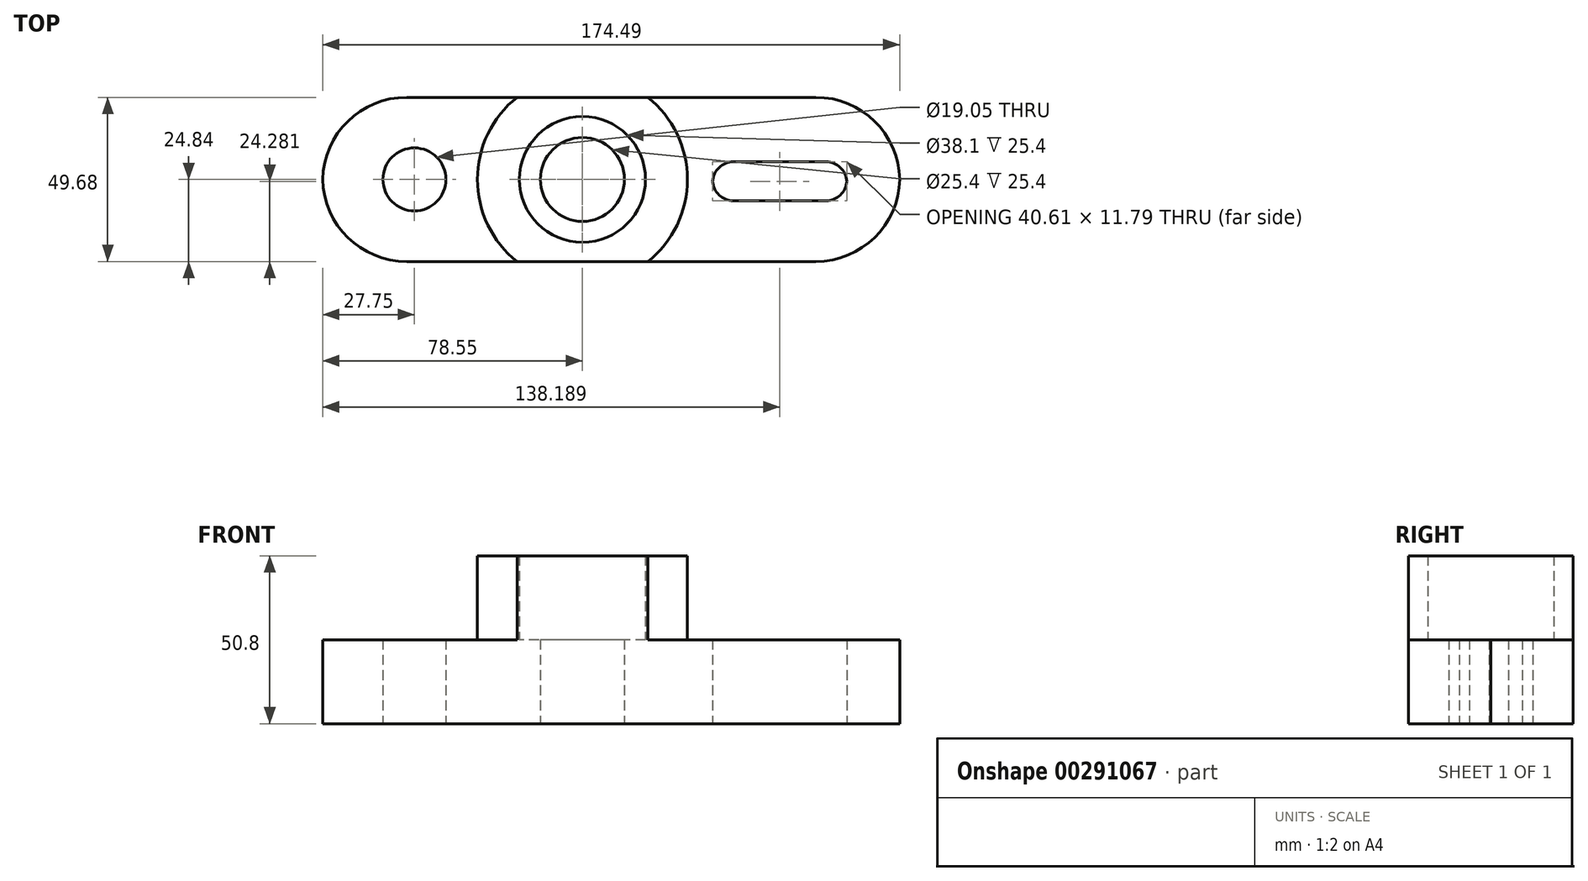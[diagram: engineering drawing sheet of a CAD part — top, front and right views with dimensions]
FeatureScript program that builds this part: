
annotation { "Feature Type Name" : "Feature", "Feature Type Description" : "" }
export const myFeature = defineFeature(function(context is Context, id is Id, definition is map)
    precondition{}
    {
        {
            var Q0;
            Q0=qCreatedBy(makeId("Top.planeOp"),FACE);
            var sketch = newSketch(context, id + "F0", { "sketchPlane" : qUnion([Q0])});
            skCircle(sketch, "E0", {"center": v(0, 0) * mm, "radius": 12.7 * mm});
            skCircle(sketch, "E1", {"center": v(0, 0) * mm, "radius": 19.05 * mm});
            skCircle(sketch, "E2", {"center": v(0, 0) * mm, "radius": 31.75 * mm});
            skCircle(sketch, "E3", {"center": v(-50.8, 0) * mm, "radius": 9.53 * mm});
            skLineSegment(sketch, "E4.bottom", {"start": v(-53.16, 24.84) * mm, "end": v(70.55, 24.84) * mm});
            skLineSegment(sketch, "E4.top", {"start": v(-53.16, -24.84) * mm, "end": v(70.55, -24.84) * mm});
            skArc(sketch, "E5.filletArc", {"start": v(-53.16, 24.84) * mm, "mid": v(-70.92, 17.6) * mm, "end": v(-78.55, 0) * mm});
            skArc(sketch, "E6.filletArc", {"start": v(-78.55, 0) * mm, "mid": v(-70.92, -17.6) * mm, "end": v(-53.16, -24.84) * mm});
            skArc(sketch, "E7.filletArc", {"start": v(95.94, 0) * mm, "mid": v(88.31, 17.6) * mm, "end": v(70.55, 24.84) * mm});
            skArc(sketch, "E8.filletArc", {"start": v(70.55, -24.84) * mm, "mid": v(88.31, -17.6) * mm, "end": v(95.94, 0) * mm});
            skLineSegment(sketch, "E9.bottom", {"start": v(45.67, 5.33) * mm, "end": v(73.6, 5.33) * mm});
            skLineSegment(sketch, "E9.top", {"start": v(45.67, -6.45) * mm, "end": v(73.6, -6.45) * mm});
            skArc(sketch, "E10.filletArc", {"start": v(45.67, 5.33) * mm, "mid": v(41.34, 3.63) * mm, "end": v(39.34, -0.56) * mm});
            skArc(sketch, "E11.filletArc", {"start": v(39.34, -0.56) * mm, "mid": v(41.34, -4.75) * mm, "end": v(45.67, -6.45) * mm});
            skArc(sketch, "E12.filletArc", {"start": v(79.94, -0.56) * mm, "mid": v(77.93, 3.63) * mm, "end": v(73.6, 5.33) * mm});
            skArc(sketch, "E13.filletArc", {"start": v(73.6, -6.45) * mm, "mid": v(77.93, -4.75) * mm, "end": v(79.94, -0.56) * mm});
            skSolve(sketch);
        }
        {
            var Q0;
            Q0=makeQuery(id+"F0.imprint","IMPRINT",FACE,{"disambiguationData":[TD([[makeQuery(id+"F0.imprint","IMPRINT",EDGE,{"derivedFrom":sQuery(id+"F0.wireOp",EDGE,"E3")}),-1.0]])]});
            extrude(context, id + "F1", {"entities" : qUnion([Q0]), "depth" : 25.4 * mm});
        }
        {
            var Q0;
            {var subQ0=sQuery(id+"F0.wireOp",EDGE,"E4.top");var subQ1=sQuery(id+"F0.wireOp",EDGE,"E2");var subQ2=makeQuery(id+"F0.imprint","INTERSECT",VERTEX,{"disambiguationData":[OD(0.0)],"derivedFrom":[subQ1,subQ0]});Q0=makeQuery(id+"F0.imprint","IMPRINT",FACE,{"disambiguationData":[TD([[makeQuery(id+"F0.imprint","IMPRINT",EDGE,{"disambiguationData":[TD([[subQ2,-1.0]])],"derivedFrom":subQ1}),1.0]])]});}
            var Q1;
            {var subQ0=sQuery(id+"F0.wireOp",EDGE,"E4.bottom");var subQ1=sQuery(id+"F0.wireOp",EDGE,"E2");var subQ2=makeQuery(id+"F0.imprint","INTERSECT",VERTEX,{"disambiguationData":[OD(0.0)],"derivedFrom":[subQ1,subQ0]});Q1=makeQuery(id+"F0.imprint","IMPRINT",FACE,{"disambiguationData":[TD([[makeQuery(id+"F0.imprint","IMPRINT",EDGE,{"disambiguationData":[TD([[subQ2,1.0]])],"derivedFrom":subQ1}),1.0]])]});}
            var Q2;
            Q2=makeQuery(id+"F0.imprint","IMPRINT",FACE,{"disambiguationData":[TD([[makeQuery(id+"F0.imprint","IMPRINT",EDGE,{"derivedFrom":sQuery(id+"F0.wireOp",EDGE,"E1")}),-1.0]])]});
            extrude(context, id + "F2", {"entities" : qUnion([Q0, Q1, Q2]), "operationType" : NewBodyOperationType.ADD, "depth" : 50.8 * mm});
        }
        {
            var Q0;
            {var subQ6=sQuery(id+"F0.wireOp",EDGE,"E7.filletArc");Q0=makeQuery(id+"F0.imprint","IMPRINT",FACE,{"disambiguationData":[TD([[makeQuery(id+"F0.imprint","IMPRINT",EDGE,{"derivedFrom":subQ6}),1.0]])]});}
            var Q1;
            Q1=makeQuery(id+"F0.imprint","IMPRINT",FACE,{"disambiguationData":[TD([[makeQuery(id+"F0.imprint","IMPRINT",EDGE,{"derivedFrom":sQuery(id+"F0.wireOp",EDGE,"E0")}),-1.0]])]});
            extrude(context, id + "F3", {"entities" : qUnion([Q0, Q1]), "operationType" : NewBodyOperationType.ADD, "depth" : 25.4 * mm});
        }
    });
